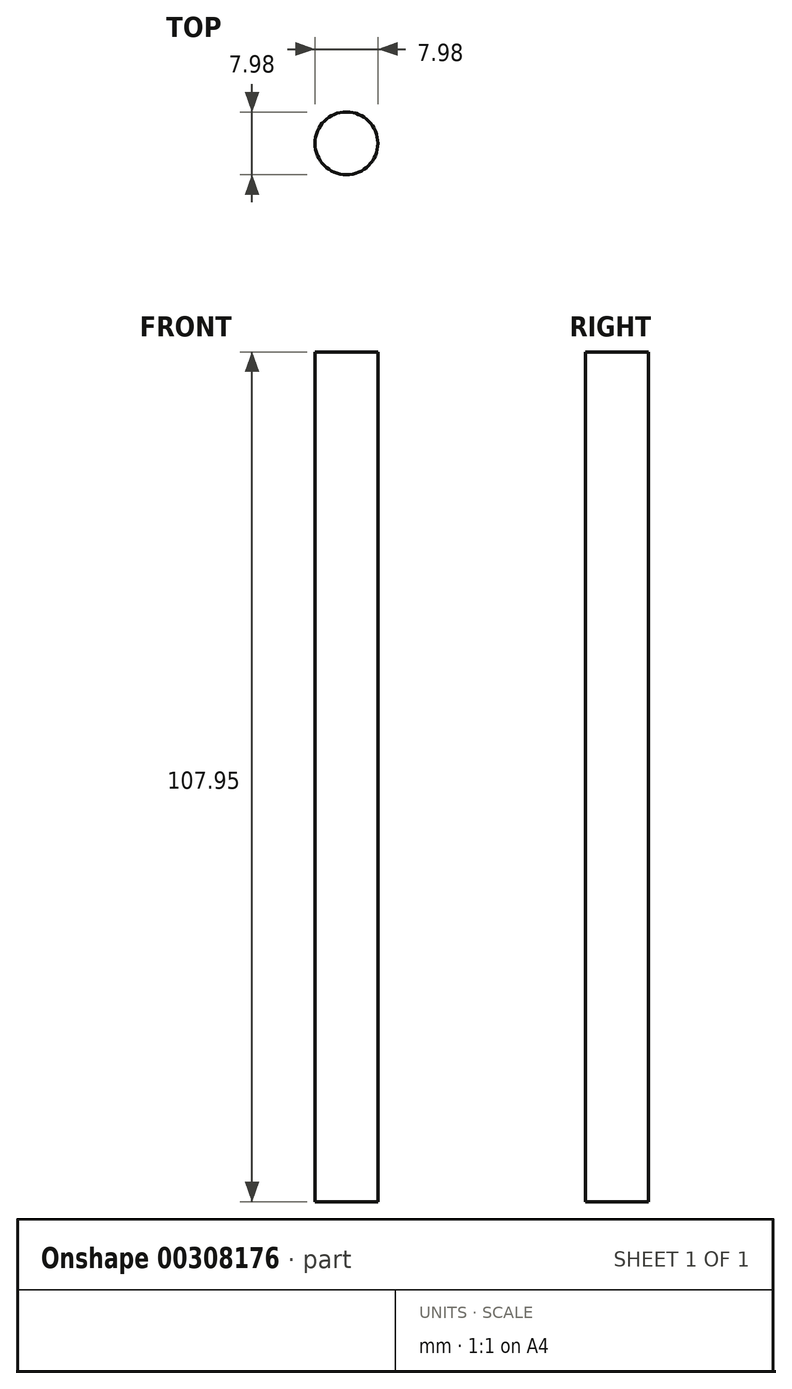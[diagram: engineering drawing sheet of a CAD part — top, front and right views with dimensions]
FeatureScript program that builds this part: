
annotation { "Feature Type Name" : "Feature", "Feature Type Description" : "" }
export const myFeature = defineFeature(function(context is Context, id is Id, definition is map)
    precondition{}
    {
        {
            var Q0;
            Q0=qCreatedBy(makeId("Top.planeOp"),FACE);
            var sketch = newSketch(context, id + "F0", { "sketchPlane" : qUnion([Q0])});
            skCircle(sketch, "E0", {"center": v(0, 0) * mm, "radius": 3.99 * mm});
            skSolve(sketch);
        }
        {
            var Q0;
            Q0=makeQuery(id+"F0.imprint","IMPRINT",FACE,{"disambiguationData":[TD([[makeQuery(id+"F0.imprint","IMPRINT",EDGE,{"derivedFrom":sQuery(id+"F0.wireOp",EDGE,"E0")}),1.0]])]});
            extrude(context, id + "F1", {"entities" : qUnion([Q0]), "depth" : 107.95 * mm});
        }
    });
